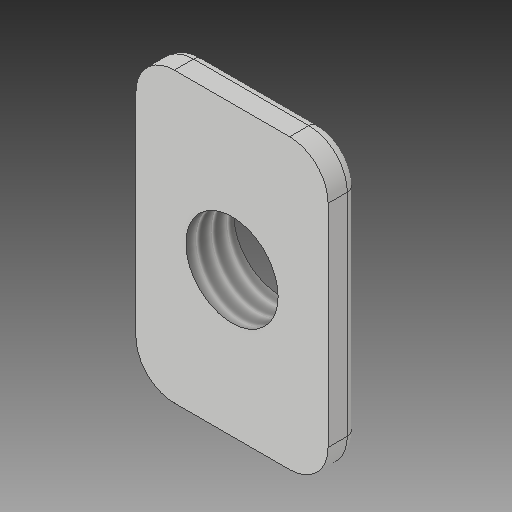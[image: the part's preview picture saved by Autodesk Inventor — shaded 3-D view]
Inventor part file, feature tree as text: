
AUTODESK INVENTOR PART (.ipt)
format: ipt  version: 2018 (Build 220112000, 112)  size: 145,920 bytes
history: native  units: mm
features: other x3, sketch x2
ambient origin geometry x8: Origin, YZ Plane, XZ Plane, XY Plane, X Axis, Y Axis, Z Axis, Center Point
bodies: Solid1 (feature_tree)
feature tree (5):
  other  "M5 Tee Nut_CPY.ipt"
  other  "Solid1::M5 Tee Nut_CPY.ipt"
  other  "TaggingFeature1"
  sketch  "Sketch1"  dims[d0=10.0mm]
  sketch  "Sketch2"
